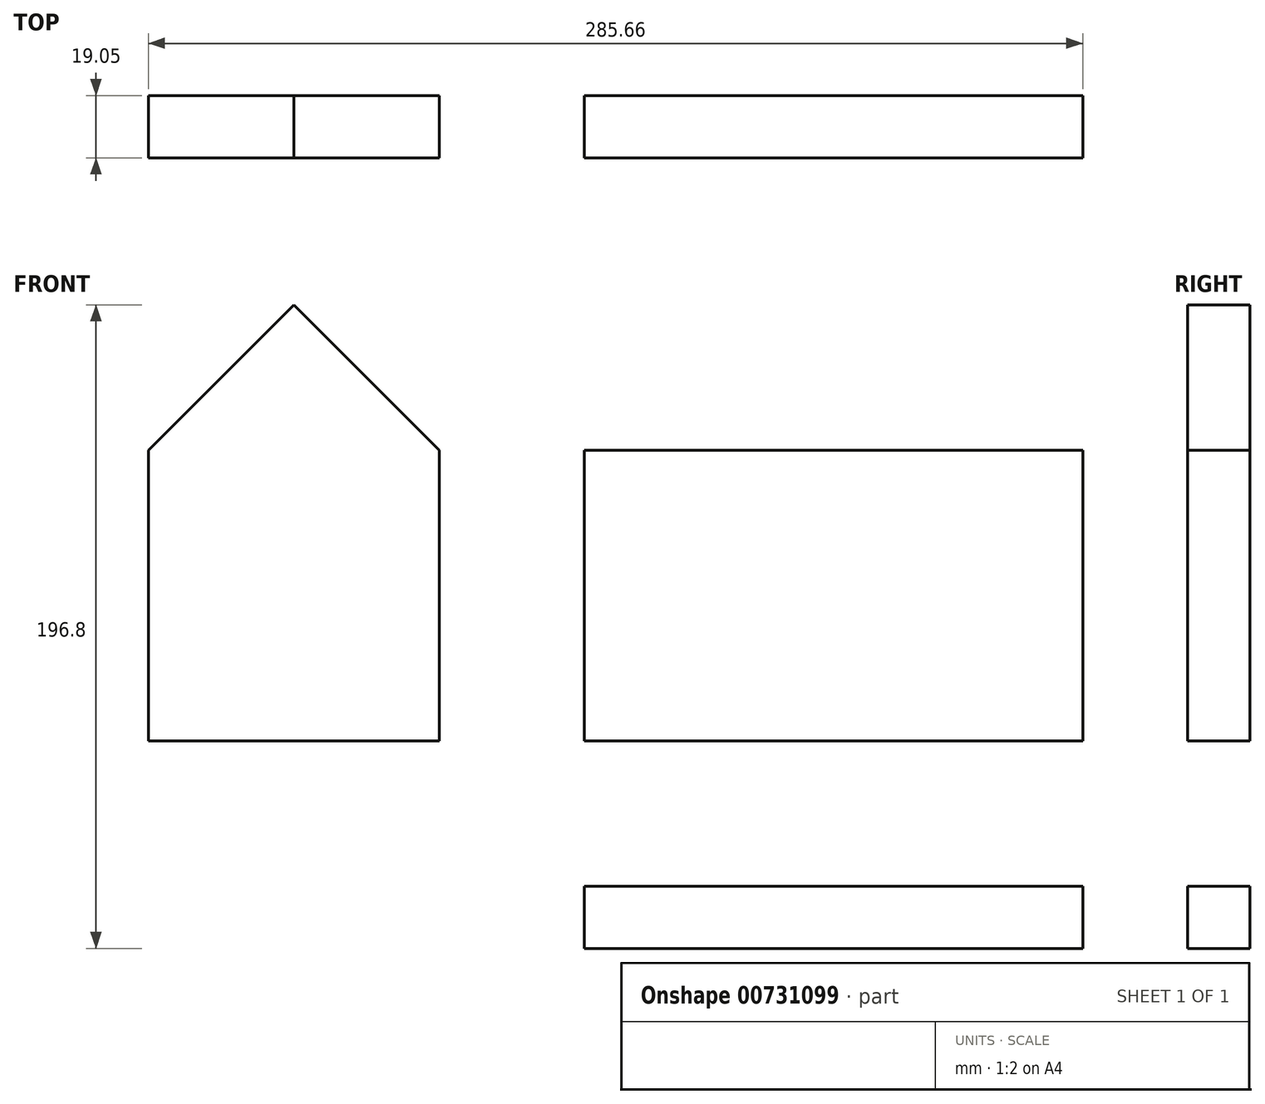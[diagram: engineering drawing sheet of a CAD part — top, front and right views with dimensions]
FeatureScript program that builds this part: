
annotation { "Feature Type Name" : "Feature", "Feature Type Description" : "" }
export const myFeature = defineFeature(function(context is Context, id is Id, definition is map)
    precondition{}
    {
        {
            var Q0;
            Q0=qCreatedBy(makeId("Front.planeOp"),FACE);
            var sketch = newSketch(context, id + "F0", { "sketchPlane" : qUnion([Q0])});
            skLineSegment(sketch, "E0.bottom", {"start": v(0, 0) * mm, "end": v(152.4, 0) * mm});
            skLineSegment(sketch, "E0.top", {"start": v(0, 88.9) * mm, "end": v(152.4, 88.9) * mm});
            skLineSegment(sketch, "E0.left", {"start": v(0, 0) * mm, "end": v(0, 88.9) * mm});
            skLineSegment(sketch, "E0.right", {"start": v(152.4, 0) * mm, "end": v(152.4, 88.9) * mm});
            skSolve(sketch);
        }
        {
            var Q0;
            Q0 = qSketchRegion(id + "F0", true);
            extrude(context, id + "F1", {"entities" : qUnion([Q0]), "depth" : 19.05 * mm, "offsetDistance" : 25.4 * mm});
        }
        {
            var Q0;
            Q0=qCreatedBy(makeId("Front.planeOp"),FACE);
            var sketch = newSketch(context, id + "F2", { "sketchPlane" : qUnion([Q0])});
            skLineSegment(sketch, "E1.bottom", {"start": v(-44.36, 0) * mm, "end": v(-133.26, 0) * mm});
            skLineSegment(sketch, "E1.top", {"start": v(-44.36, 133.35) * mm, "end": v(-133.26, 133.35) * mm});
            skLineSegment(sketch, "E1.left", {"start": v(-44.36, 0) * mm, "end": v(-44.36, 133.35) * mm});
            skLineSegment(sketch, "E1.right", {"start": v(-133.26, 0) * mm, "end": v(-133.26, 133.35) * mm});
            skSolve(sketch);
        }
        {
            var Q0;
            Q0 = qSketchRegion(id + "F2", true);
            extrude(context, id + "F3", {"entities" : qUnion([Q0]), "depth" : 19.05 * mm, "offsetDistance" : 25.4 * mm});
        }
        {
            var Q0;
            Q0=makeQuery(id+"F3.opExtrude","CAP_FACE",FACE,{"disambiguationData":[OSD([sQuery(id+"F2.wireOp",EDGE,"E1.bottom"),sQuery(id+"F2.wireOp",EDGE,"E1.top"),sQuery(id+"F2.wireOp",EDGE,"E1.left"),sQuery(id+"F2.wireOp",EDGE,"E1.right")])],"isStart":false});
            var sketch = newSketch(context, id + "F4", { "sketchPlane" : qUnion([Q0])});
            skLineSegment(sketch, "E2", {"start": v(-88.8, 133.35) * mm, "end": v(-88.8, 0) * mm, "construction": true});
            skLineSegment(sketch, "E3", {"start": v(-88.8, 133.35) * mm, "end": v(-133.26, 88.9) * mm});
            skLineSegment(sketch, "E4", {"start": v(-133.26, 88.9) * mm, "end": v(-133.26, 133.35) * mm});
            skLineSegment(sketch, "E5", {"start": v(-133.26, 133.35) * mm, "end": v(-44.36, 133.35) * mm});
            skLineSegment(sketch, "E6", {"start": v(-44.36, 133.35) * mm, "end": v(-44.36, 88.9) * mm});
            skLineSegment(sketch, "E7", {"start": v(-44.36, 88.9) * mm, "end": v(-88.8, 133.35) * mm});
            skSolve(sketch);
        }
        {
            var Q0;
            Q0 = qSketchRegion(id + "F4", true);
            extrude(context, id + "F5", {"entities" : qUnion([Q0]), "operationType" : NewBodyOperationType.REMOVE, "endBound" : BoundingType.THROUGH_ALL, "oppositeDirection" : true, "depth" : 25.4 * mm, "offsetDistance" : 25.4 * mm});
        }
        {
            var Q0;
            Q0=qCreatedBy(makeId("Front.planeOp"),FACE);
            var sketch = newSketch(context, id + "F6", { "sketchPlane" : qUnion([Q0])});
            skLineSegment(sketch, "E8.bottom", {"start": v(0, -44.4) * mm, "end": v(152.4, -44.4) * mm});
            skLineSegment(sketch, "E8.top", {"start": v(0, -63.45) * mm, "end": v(152.4, -63.45) * mm});
            skLineSegment(sketch, "E8.left", {"start": v(0, -44.4) * mm, "end": v(0, -63.45) * mm});
            skLineSegment(sketch, "E8.right", {"start": v(152.4, -44.4) * mm, "end": v(152.4, -63.45) * mm});
            skSolve(sketch);
        }
        {
            var Q0;
            Q0 = qSketchRegion(id + "F6", true);
            extrude(context, id + "F7", {"entities" : qUnion([Q0]), "depth" : 19.05 * mm, "offsetDistance" : 25.4 * mm});
        }
    });
